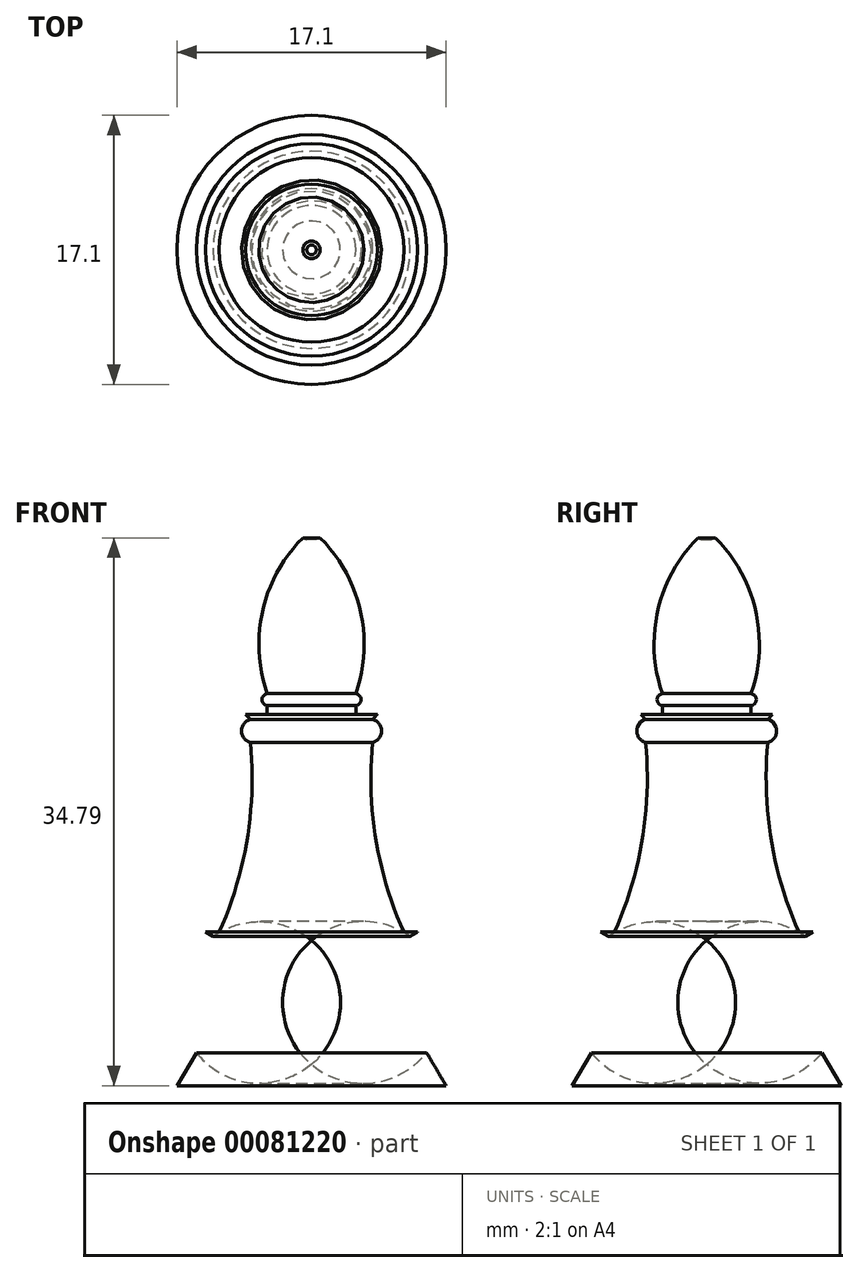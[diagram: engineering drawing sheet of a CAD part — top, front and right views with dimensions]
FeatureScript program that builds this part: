
annotation { "Feature Type Name" : "Feature", "Feature Type Description" : "" }
export const myFeature = defineFeature(function(context is Context, id is Id, definition is map)
    precondition{}
    {
        {
            var Q0;
            Q0=qCreatedBy(makeId("Right.planeOp"),FACE);
            var sketch = newSketch(context, id + "F0", { "sketchPlane" : qUnion([Q0])});
            skLineSegment(sketch, "E0", {"start": v(-6.26, -15.84) * mm, "end": v(-6.74, -15.57) * mm});
            skLineSegment(sketch, "E1", {"start": v(-6.74, -15.57) * mm, "end": v(-5.86, -15.57) * mm});
            skArc(sketch, "E2", {"start": v(-5.86, -15.57) * mm, "mid": v(-4.09, -9.67) * mm, "end": v(-3.88, -3.51) * mm});
            skArc(sketch, "E3", {"start": v(-3.88, -2.06) * mm, "mid": v(-4.44, -2.79) * mm, "end": v(-3.88, -3.51) * mm});
            skLineSegment(sketch, "E4", {"start": v(-3.88, -2.06) * mm, "end": v(-4.18, -1.73) * mm});
            skLineSegment(sketch, "E5", {"start": v(-4.18, -1.73) * mm, "end": v(-2.82, -1.73) * mm});
            skLineSegment(sketch, "E6", {"start": v(-2.82, -1.73) * mm, "end": v(-2.82, -1.18) * mm});
            skArc(sketch, "E7", {"start": v(-2.82, -0.42) * mm, "mid": v(-3.15, -0.8) * mm, "end": v(-2.82, -1.18) * mm});
            skArc(sketch, "E8", {"start": v(0, 10.87) * mm, "mid": v(-0.86, 10.4) * mm, "end": v(-0.55, 9.47) * mm});
            skLineSegment(sketch, "E9", {"start": v(0, 10.87) * mm, "end": v(0, -25.32) * mm});
            skArc(sketch, "E10", {"start": v(-6.26, -15.84) * mm, "mid": v(-8.38, -19.3) * mm, "end": v(-7.31, -23.23) * mm});
            skLineSegment(sketch, "E11", {"start": v(0, -25.32) * mm, "end": v(-8.55, -25.32) * mm});
            skLineSegment(sketch, "E12", {"start": v(-8.55, -25.32) * mm, "end": v(-7.31, -23.23) * mm});
            skArc(sketch, "E13", {"start": v(-0.55, 9.47) * mm, "mid": v(-3.1, 4.85) * mm, "end": v(-2.82, -0.42) * mm});
            skSolve(sketch);
        }
        {
            var Q0;
            Q0 = qSketchRegion(id + "F0", true);
            var Q1;
            Q1=sQuery(id+"F0.wireOp",EDGE,"E9");
            revolve(context, id + "F1", {"entities" : qUnion([Q0]), "axis" : qUnion([Q1]), "revolveType" : RevolveType.FULL});
        }
    });
